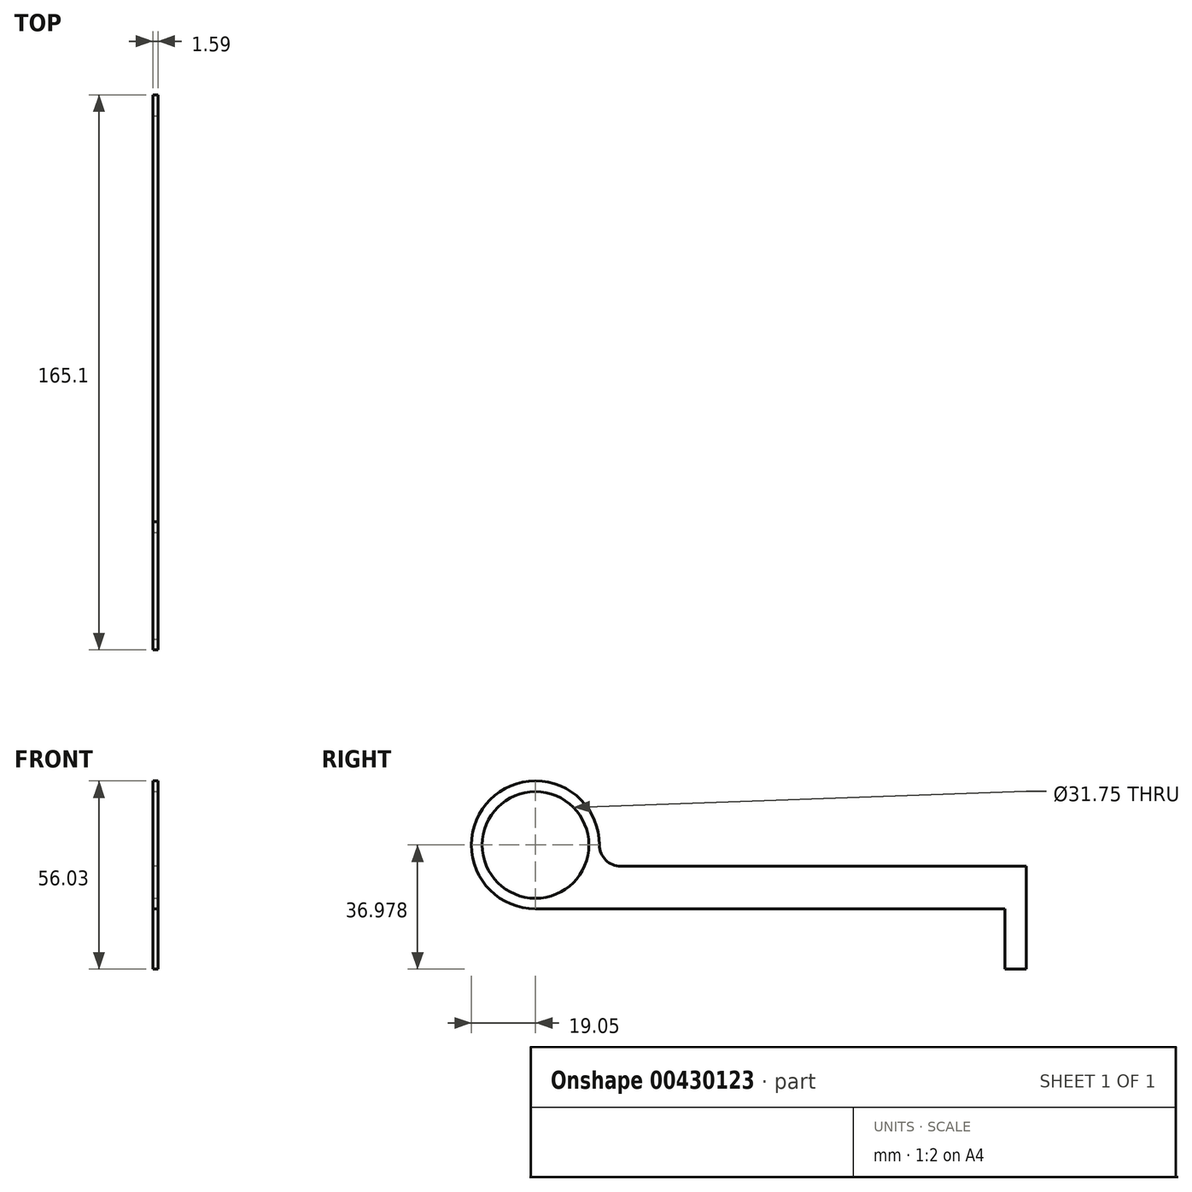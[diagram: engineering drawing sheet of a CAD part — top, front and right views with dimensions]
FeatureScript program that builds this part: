
annotation { "Feature Type Name" : "Feature", "Feature Type Description" : "" }
export const myFeature = defineFeature(function(context is Context, id is Id, definition is map)
    precondition{}
    {
        {
            var Q0;
            Q0=qCreatedBy(makeId("Right.planeOp"),FACE);
            var sketch = newSketch(context, id + "F0", { "sketchPlane" : qUnion([Q0])});
            skLineSegment(sketch, "E0", {"start": v(81.24, 16.59) * mm, "end": v(-77.51, 16.59) * mm});
            skLineSegment(sketch, "E1", {"start": v(-77.51, 16.59) * mm, "end": v(-77.51, 54.69) * mm});
            skLineSegment(sketch, "E2", {"start": v(-77.51, 54.69) * mm, "end": v(-39.41, 54.69) * mm});
            skLineSegment(sketch, "E3", {"start": v(-39.41, 54.69) * mm, "end": v(-39.41, 29.29) * mm});
            skLineSegment(sketch, "E4", {"start": v(-39.41, 29.29) * mm, "end": v(87.59, 29.29) * mm});
            skLineSegment(sketch, "E5", {"start": v(87.59, 29.29) * mm, "end": v(87.59, -1.34) * mm});
            skLineSegment(sketch, "E6", {"start": v(81.24, 16.59) * mm, "end": v(81.24, -1.34) * mm});
            skLineSegment(sketch, "E7", {"start": v(81.24, -1.34) * mm, "end": v(87.59, -1.34) * mm});
            skSolve(sketch);
        }
        {
            var Q0;
            Q0=makeQuery(id+"F0.imprint","IMPRINT",FACE,{"disambiguationData":[TD([[makeQuery(id+"F0.imprint","IMPRINT",EDGE,{"derivedFrom":sQuery(id+"F0.wireOp",EDGE,"E0")}),-1.0]])]});
            extrude(context, id + "F1", {"entities" : qUnion([Q0]), "depth" : 1.59 * mm});
        }
        {
            var Q0;
            Q0=makeQuery(id+"F1.opExtrude","SWEPT_EDGE",EDGE,{"disambiguationData":[OSD([sQuery(id+"F0.wireOp",EDGE,"E1"),sQuery(id+"F0.wireOp",EDGE,"E2")])]});
            var Q1;
            Q1=makeQuery(id+"F1.opExtrude","SWEPT_EDGE",EDGE,{"disambiguationData":[OSD([sQuery(id+"F0.wireOp",EDGE,"E0"),sQuery(id+"F0.wireOp",EDGE,"E1")])]});
            var Q2;
            Q2=makeQuery(id+"F1.opExtrude","SWEPT_EDGE",EDGE,{"disambiguationData":[OSD([sQuery(id+"F0.wireOp",EDGE,"E2"),sQuery(id+"F0.wireOp",EDGE,"E3")])]});
            fillet(context, id + "F2", {"entities" : qUnion([Q0, Q1, Q2]), "radius" : 19.05 * mm, "tangentPropagation" : true, "allowEdgeOverflow" : false});
        }
        {
            var Q0;
            Q0=makeQuery(id+"F1.opExtrude","SWEPT_EDGE",EDGE,{"disambiguationData":[OSD([sQuery(id+"F0.wireOp",EDGE,"E3"),sQuery(id+"F0.wireOp",EDGE,"E4")])]});
            fillet(context, id + "F3", {"entities" : qUnion([Q0]), "radius" : 6.35 * mm, "tangentPropagation" : true, "allowEdgeOverflow" : false});
        }
        {
            var Q0;
            Q0=makeQuery(id+"F1.opExtrude","CAP_FACE",FACE,{"disambiguationData":[OSD([sQuery(id+"F0.wireOp",EDGE,"E0"),sQuery(id+"F0.wireOp",EDGE,"E1"),sQuery(id+"F0.wireOp",EDGE,"E2"),sQuery(id+"F0.wireOp",EDGE,"E3"),sQuery(id+"F0.wireOp",EDGE,"E4"),sQuery(id+"F0.wireOp",EDGE,"E5"),sQuery(id+"F0.wireOp",EDGE,"E6"),sQuery(id+"F0.wireOp",EDGE,"E7")])],"isStart":false});
            var sketch = newSketch(context, id + "F4", { "sketchPlane" : qUnion([Q0])});
            skCircle(sketch, "E8", {"center": v(-58.46, 35.64) * mm, "radius": 15.88 * mm});
            skSolve(sketch);
        }
        {
            var Q0;
            Q0=qSketchRegion(id+"F4",true);
            extrude(context, id + "F5", {"entities" : qUnion([Q0]), "operationType" : NewBodyOperationType.REMOVE, "oppositeDirection" : true, "depth" : 25.4 * mm});
        }
    });
